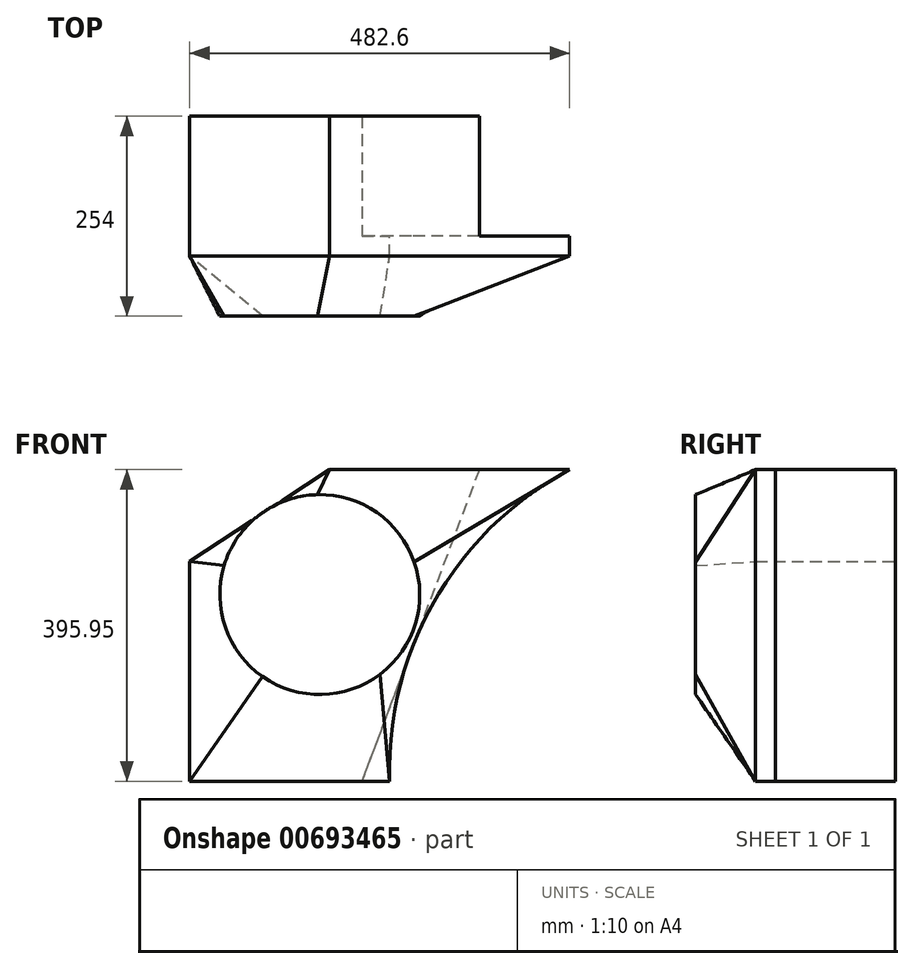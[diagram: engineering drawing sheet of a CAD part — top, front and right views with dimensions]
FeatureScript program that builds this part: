
annotation { "Feature Type Name" : "Feature", "Feature Type Description" : "" }
export const myFeature = defineFeature(function(context is Context, id is Id, definition is map)
    precondition{}
    {
        {
            var Q0;
            Q0=qCreatedBy(makeId("Front.planeOp"),FACE);
            var sketch = newSketch(context, id + "F0", { "sketchPlane" : qUnion([Q0])});
            skLineSegment(sketch, "E0", {"start": v(0, 0) * mm, "end": v(254, 0) * mm});
            skLineSegment(sketch, "E1", {"start": v(482.6, 395.95) * mm, "end": v(177.8, 395.95) * mm});
            skLineSegment(sketch, "E2", {"start": v(177.8, 395.95) * mm, "end": v(0, 279.4) * mm});
            skLineSegment(sketch, "E3", {"start": v(0, 279.4) * mm, "end": v(0, 0) * mm});
            skArc(sketch, "E4", {"start": v(482.6, 395.95) * mm, "mid": v(311.6, 230.71) * mm, "end": v(254, 0) * mm});
            skSolve(sketch);
        }
        {
            var Q0;
            Q0=makeQuery(id+"F0.imprint","IMPRINT",FACE,{"disambiguationData":[TD([[makeQuery(id+"F0.imprint","IMPRINT",EDGE,{"derivedFrom":sQuery(id+"F0.wireOp",EDGE,"E0")}),1.0]])]});
            extrude(context, id + "F1", {"entities" : qUnion([Q0]), "depth" : 25.4 * mm, "offsetDistance" : 25.4 * mm});
        }
        {
            var Q0;
            Q0=makeQuery(id+"F1.opExtrude","CAP_FACE",FACE,{"disambiguationData":[OSD([sQuery(id+"F0.wireOp",EDGE,"E0"),sQuery(id+"F0.wireOp",EDGE,"E1"),sQuery(id+"F0.wireOp",EDGE,"E2"),sQuery(id+"F0.wireOp",EDGE,"E3"),sQuery(id+"F0.wireOp",EDGE,"E4")])],"isStart":false});
            cPlane(context, id + "F2", {"entities" : qUnion([Q0]), "cplaneType" : CPlaneType.OFFSET, "offset" : 76.2 * mm, "width" : 152.4 * mm, "height" : 152.4 * mm});
        }
        {
            var Q0;
            Q0=qCreatedBy(id+"F2.planeOp",FACE);
            var sketch = newSketch(context, id + "F3", { "sketchPlane" : qUnion([Q0])});
            skCircle(sketch, "E5", {"center": v(165.1, 237.2) * mm, "radius": 127 * mm});
            skSolve(sketch);
        }
        {
            var Q1;
            Q1 = qSketchRegion(id + "F3", true);
            var Q2;
            Q2=makeQuery(id+"F1.opExtrude","CAP_FACE",FACE,{"disambiguationData":[OSD([sQuery(id+"F0.wireOp",EDGE,"E0"),sQuery(id+"F0.wireOp",EDGE,"E1"),sQuery(id+"F0.wireOp",EDGE,"E2"),sQuery(id+"F0.wireOp",EDGE,"E3"),sQuery(id+"F0.wireOp",EDGE,"E4")])],"isStart":false});
            loft(context, id + "F4", {"operationType" : NewBodyOperationType.ADD, "sheetProfilesArray" : [{ "sheetProfileEntities" : qUnion([Q1]) }, { "sheetProfileEntities" : qUnion([Q2]) }]});
        }
        {
            var Q0;
            Q0=makeQuery(id+"F1.opExtrude","CAP_FACE",FACE,{"disambiguationData":[OSD([sQuery(id+"F0.wireOp",EDGE,"E0"),sQuery(id+"F0.wireOp",EDGE,"E1"),sQuery(id+"F0.wireOp",EDGE,"E2"),sQuery(id+"F0.wireOp",EDGE,"E3"),sQuery(id+"F0.wireOp",EDGE,"E4")])],"isStart":true});
            var sketch = newSketch(context, id + "F5", { "sketchPlane" : qUnion([Q0])});
            skLineSegment(sketch, "E6.0", {"start": v(0, 0) * mm, "end": v(-218.5, 0) * mm});
            skLineSegment(sketch, "E7.0", {"start": v(0, 279.4) * mm, "end": v(0, 0) * mm});
            skLineSegment(sketch, "E8.0", {"start": v(-177.8, 395.95) * mm, "end": v(0, 279.4) * mm});
            skLineSegment(sketch, "E9.0", {"start": v(-367.76, 395.95) * mm, "end": v(-177.8, 395.95) * mm});
            skLineSegment(sketch, "E10", {"start": v(-367.76, 395.95) * mm, "end": v(-218.5, 0) * mm});
            skPoint(sketch, "E11.orphan", {"position": v(-254, 0) * mm});
            skPoint(sketch, "E12.orphan", {"position": v(-482.6, 395.95) * mm});
            skSolve(sketch);
        }
        {
            var Q0;
            Q0 = qSketchRegion(id + "F5", true);
            extrude(context, id + "F6", {"entities" : qUnion([Q0]), "operationType" : NewBodyOperationType.ADD, "depth" : 152.4 * mm, "offsetDistance" : 25.4 * mm});
        }
    });
